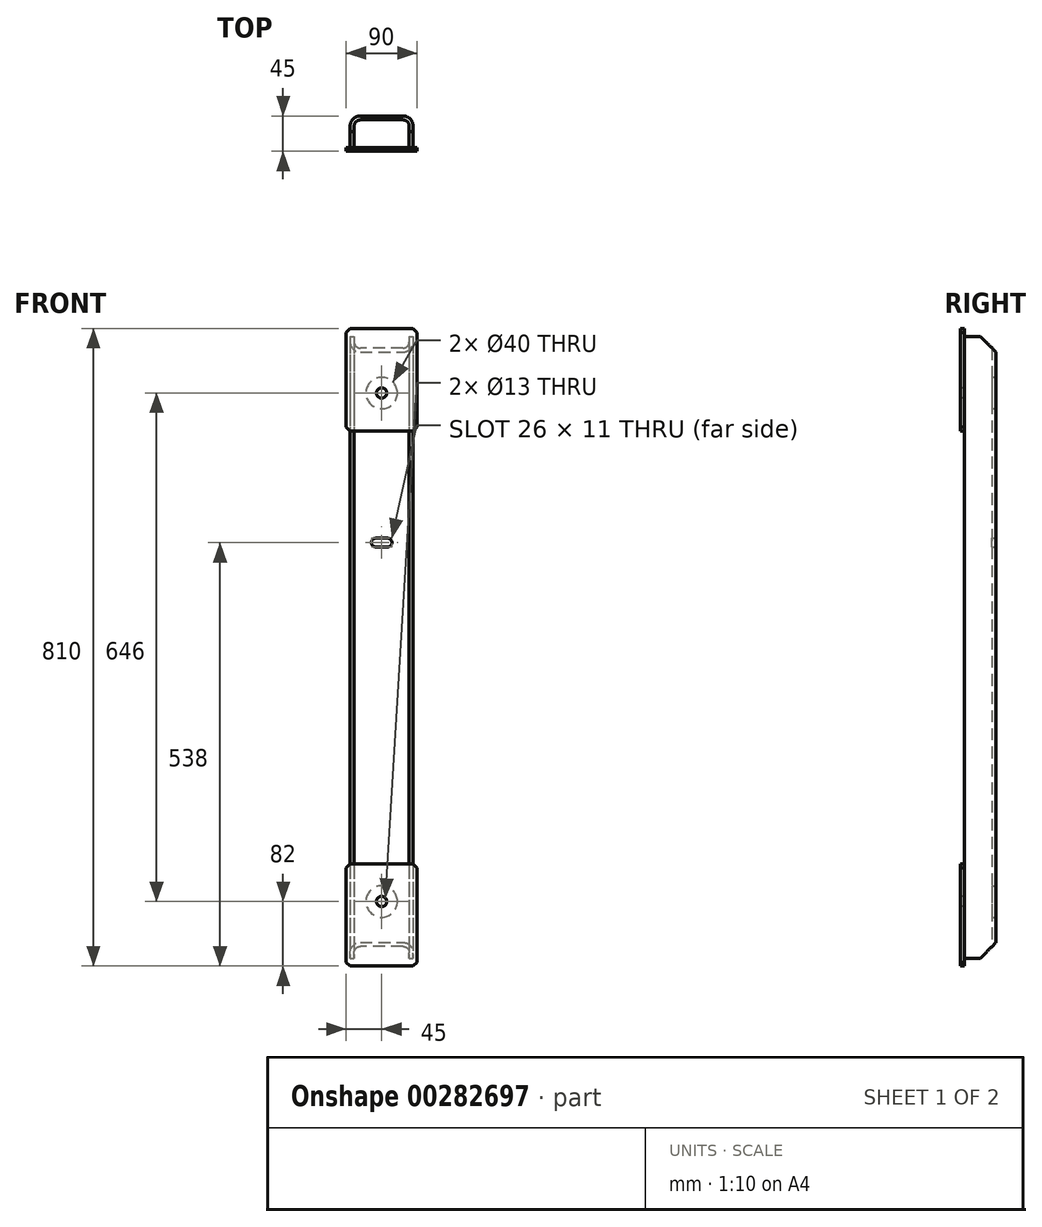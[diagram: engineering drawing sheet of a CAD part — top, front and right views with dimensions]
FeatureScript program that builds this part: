
annotation { "Feature Type Name" : "Feature", "Feature Type Description" : "" }
export const myFeature = defineFeature(function(context is Context, id is Id, definition is map)
    precondition{}
    {
        {
            var Q0;
            Q0=qCreatedBy(makeId("Top.planeOp"),FACE);
            var sketch = newSketch(context, id + "F0", { "sketchPlane" : qUnion([Q0])});
            skLineSegment(sketch, "E0.bottom", {"start": v(-27, 40) * mm, "end": v(27, 40) * mm});
            skLineSegment(sketch, "E0.top", {"start": v(-40, 0) * mm, "end": v(-35, 0) * mm});
            skLineSegment(sketch, "E0.left", {"start": v(-40, 27) * mm, "end": v(-40, 0) * mm});
            skLineSegment(sketch, "E0.right", {"start": v(40, 27) * mm, "end": v(40, 0) * mm});
            skPoint(sketch, "E0.middle", {"position": v(0, 20) * mm});
            skLineSegment(sketch, "E1.0", {"start": v(-27, 35) * mm, "end": v(27, 35) * mm});
            skLineSegment(sketch, "E1.1", {"start": v(-35, 27) * mm, "end": v(-35, 0) * mm});
            skLineSegment(sketch, "E1.3", {"start": v(35, 27) * mm, "end": v(35, 0) * mm});
            skLineSegment(sketch, "E2.trimOffspring", {"start": v(35, 0) * mm, "end": v(40, 0) * mm});
            skPoint(sketch, "E3.visualSharp", {"position": v(-35, 35) * mm});
            skArc(sketch, "E3.filletArc", {"start": v(-27, 35) * mm, "mid": v(-32.66, 32.66) * mm, "end": v(-35, 27) * mm});
            skPoint(sketch, "E4.visualSharp", {"position": v(35, 35) * mm});
            skArc(sketch, "E4.filletArc", {"start": v(35, 27) * mm, "mid": v(32.66, 32.66) * mm, "end": v(27, 35) * mm});
            skPoint(sketch, "E5.visualSharp", {"position": v(-40, 40) * mm});
            skArc(sketch, "E5.filletArc", {"start": v(-27, 40) * mm, "mid": v(-36.2, 36.2) * mm, "end": v(-40, 27) * mm});
            skPoint(sketch, "E6.visualSharp", {"position": v(40, 40) * mm});
            skArc(sketch, "E6.filletArc", {"start": v(40, 27) * mm, "mid": v(36.2, 36.2) * mm, "end": v(27, 40) * mm});
            skSolve(sketch);
        }
        {
            var Q0;
            Q0=makeQuery(id+"F0.imprint","IMPRINT",FACE,{"disambiguationData":[TD([[makeQuery(id+"F0.imprint","IMPRINT",EDGE,{"derivedFrom":sQuery(id+"F0.wireOp",EDGE,"E0.bottom")}),-1.0]])]});
            extrude(context, id + "F1", {"entities" : qUnion([Q0]), "depth" : 790 * mm, "symmetric" : true});
        }
        {
            var Q0;
            Q0=makeQuery(id+"F1.opExtrude","SWEPT_FACE",FACE,{"disambiguationData":[OSD([sQuery(id+"F0.wireOp",EDGE,"E0.bottom")])]});
            var sketch = newSketch(context, id + "F2", { "sketchPlane" : qUnion([Q0])});
            skLineSegment(sketch, "E7", {"start": v(0, 395) * mm, "end": v(0, -395) * mm, "construction": true});
            skCircle(sketch, "E8", {"center": v(0, 323) * mm, "radius": 20 * mm});
            skCircle(sketch, "E9", {"center": v(0, -323) * mm, "radius": 20 * mm});
            skLineSegment(sketch, "E10", {"start": v(79.25, 133) * mm, "end": v(-83.9, 133) * mm, "construction": true});
            skArc(sketch, "E11", {"start": v(7.5, 127.5) * mm, "mid": v(13, 133) * mm, "end": v(7.5, 138.5) * mm});
            skArc(sketch, "E12", {"start": v(-7.5, 138.5) * mm, "mid": v(-13, 133) * mm, "end": v(-7.5, 127.5) * mm});
            skLineSegment(sketch, "E13", {"start": v(7.5, 138.5) * mm, "end": v(-7.5, 138.5) * mm});
            skLineSegment(sketch, "E14", {"start": v(7.5, 127.5) * mm, "end": v(-7.5, 127.5) * mm});
            skArc(sketch, "E15.MirrorCS", {"start": v(-7.5, -138.5) * mm, "mid": v(-13, -133) * mm, "end": v(-7.5, -127.5) * mm});
            skArc(sketch, "E16.MirrorCS", {"start": v(7.5, -127.5) * mm, "mid": v(13, -133) * mm, "end": v(7.5, -138.5) * mm});
            skLineSegment(sketch, "E17.MirrorCS", {"start": v(7.5, -127.5) * mm, "end": v(-7.5, -127.5) * mm});
            skLineSegment(sketch, "E18.MirrorCS", {"start": v(7.5, -138.5) * mm, "end": v(-7.5, -138.5) * mm});
            skSolve(sketch);
        }
        {
            var Q0;
            Q0=makeQuery(id+"F2.imprint","IMPRINT",FACE,{"disambiguationData":[TD([[makeQuery(id+"F2.imprint","IMPRINT",EDGE,{"derivedFrom":sQuery(id+"F2.wireOp",EDGE,"E8")}),1.0]])]});
            var Q1;
            Q1=makeQuery(id+"F2.imprint","IMPRINT",FACE,{"disambiguationData":[TD([[makeQuery(id+"F2.imprint","IMPRINT",EDGE,{"derivedFrom":sQuery(id+"F2.wireOp",EDGE,"E11")}),1.0]])]});
            var Q2;
            Q2=makeQuery(id+"F2.imprint","IMPRINT",FACE,{"disambiguationData":[TD([[makeQuery(id+"F2.imprint","IMPRINT",EDGE,{"derivedFrom":sQuery(id+"F2.wireOp",EDGE,"E15.MirrorCS")}),-1.0]])]});
            var Q3;
            Q3=makeQuery(id+"F2.imprint","IMPRINT",FACE,{"disambiguationData":[TD([[makeQuery(id+"F2.imprint","IMPRINT",EDGE,{"derivedFrom":sQuery(id+"F2.wireOp",EDGE,"E9")}),1.0]])]});
            extrude(context, id + "F3", {"entities" : qUnion([Q0, Q1, Q2, Q3]), "operationType" : NewBodyOperationType.REMOVE, "endBound" : BoundingType.THROUGH_ALL, "oppositeDirection" : true, "depth" : 25 * mm});
        }
        {
            var Q0;
            Q0=makeQuery(id+"F1.opExtrude","SWEPT_FACE",FACE,{"disambiguationData":[OSD([sQuery(id+"F0.wireOp",EDGE,"E0.top")])]});
            var sketch = newSketch(context, id + "F4", { "sketchPlane" : qUnion([Q0])});
            skLineSegment(sketch, "E19.bottom", {"start": v(-45, 405) * mm, "end": v(45, 405) * mm});
            skLineSegment(sketch, "E19.top", {"start": v(-45, 275) * mm, "end": v(45, 275) * mm});
            skLineSegment(sketch, "E19.left", {"start": v(-45, 405) * mm, "end": v(-45, 275) * mm});
            skLineSegment(sketch, "E19.right", {"start": v(45, 405) * mm, "end": v(45, 275) * mm});
            skSolve(sketch);
        }
        {
            var Q0;
            Q0=makeQuery(id+"F4.imprint","IMPRINT",FACE,{"disambiguationData":[TD([[makeQuery(id+"F4.imprint","IMPRINT",EDGE,{"derivedFrom":sQuery(id+"F4.wireOp",EDGE,"E19.bottom")}),-1.0]])]});
            var Q1;
            {var subQ1=sQuery(id+"F0.wireOp",EDGE,"E0.top");var subQ6=makeQuery(id+"F1.opExtrude","CAP_EDGE",EDGE,{"disambiguationData":[OSD([subQ1])],"isStart":false});Q1=makeQuery(id+"F4.imprint","IMPRINT",FACE,{"disambiguationData":[TD([[makeQuery(id+"F4.imprint","IMPRINT",EDGE,{"derivedFrom":subQ6}),-1.0]])]});}
            extrude(context, id + "F5", {"entities" : qUnion([Q0, Q1]), "depth" : 5 * mm});
        }
        {
            var Q0;
            Q0=makeQuery(id+"F5.opExtrude","SWEPT_EDGE",EDGE,{"disambiguationData":[OSD([sQuery(id+"F4.wireOp",EDGE,"E19.top"),sQuery(id+"F4.wireOp",EDGE,"E19.right")])]});
            var Q1;
            Q1=makeQuery(id+"F5.opExtrude","SWEPT_EDGE",EDGE,{"disambiguationData":[OSD([sQuery(id+"F4.wireOp",EDGE,"E19.top"),sQuery(id+"F4.wireOp",EDGE,"E19.left")])]});
            var Q2;
            Q2=makeQuery(id+"F5.opExtrude","SWEPT_EDGE",EDGE,{"disambiguationData":[OSD([sQuery(id+"F4.wireOp",EDGE,"E19.bottom"),sQuery(id+"F4.wireOp",EDGE,"E19.left")])]});
            var Q3;
            Q3=makeQuery(id+"F5.opExtrude","SWEPT_EDGE",EDGE,{"disambiguationData":[OSD([sQuery(id+"F4.wireOp",EDGE,"E19.bottom"),sQuery(id+"F4.wireOp",EDGE,"E19.right")])]});
            chamfer(context, id + "F6", {"entities" : qUnion([Q0, Q1, Q2, Q3]), "width" : 5 * mm, "tangentPropagation" : true});
        }
        {
            var Q0;
            Q0=makeQuery(id+"F5.opExtrude","CAP_FACE",FACE,{"disambiguationData":[OSD([sQuery(id+"F4.wireOp",EDGE,"E19.bottom"),sQuery(id+"F4.wireOp",EDGE,"E19.top"),sQuery(id+"F4.wireOp",EDGE,"E19.left"),sQuery(id+"F4.wireOp",EDGE,"E19.right")])],"isStart":false});
            var sketch = newSketch(context, id + "F7", { "sketchPlane" : qUnion([Q0])});
            skCircle(sketch, "E20.0", {"center": v(0, 323) * mm, "radius": 20 * mm});
            skCircle(sketch, "E21", {"center": v(0, 323) * mm, "radius": 6.5 * mm});
            skSolve(sketch);
        }
        {
            var Q0;
            Q0=makeQuery(id+"F7.imprint","IMPRINT",FACE,{"disambiguationData":[TD([[makeQuery(id+"F7.imprint","IMPRINT",EDGE,{"derivedFrom":sQuery(id+"F7.wireOp",EDGE,"E21")}),1.0]])]});
            extrude(context, id + "F8", {"entities" : qUnion([Q0]), "operationType" : NewBodyOperationType.REMOVE, "endBound" : BoundingType.THROUGH_ALL, "oppositeDirection" : true, "depth" : 25 * mm});
        }
        {
            var Q0;
            Q0=makeQuery(id+"F5.opExtrude","SWEPT_BODY",BODY,{"disambiguationData":[OSD([sQuery(id+"F4.wireOp",EDGE,"E19.bottom"),sQuery(id+"F4.wireOp",EDGE,"E19.top"),sQuery(id+"F4.wireOp",EDGE,"E19.left"),sQuery(id+"F4.wireOp",EDGE,"E19.right")])]});
            var Q1;
            Q1=qCreatedBy(makeId("Top.planeOp"),FACE);
            mirror(context, id + "F9", {"operationType" : NewBodyOperationType.ADD, "entities" : qUnion([Q0]), "mirrorPlane" : qUnion([Q1])});
        }
        {
            var Q0;
            Q0=makeQuery(id+"F1.opExtrude","SWEPT_FACE",FACE,{"disambiguationData":[OSD([sQuery(id+"F0.wireOp",EDGE,"E0.right")])]});
            var sketch = newSketch(context, id + "F10", { "sketchPlane" : qUnion([Q0])});
            skLineSegment(sketch, "E22.0", {"start": v(40, 395) * mm, "end": v(20, 395) * mm});
            skLineSegment(sketch, "E22.1", {"start": v(40, 395) * mm, "end": v(40, 375) * mm});
            skPoint(sketch, "E23.orphan", {"position": v(27, 395) * mm});
            skLineSegment(sketch, "E24", {"start": v(20, 395) * mm, "end": v(40, 375) * mm});
            skPoint(sketch, "E25.orphan", {"position": v(40, -395) * mm});
            skPoint(sketch, "E26.orphan", {"position": v(0, 395) * mm});
            skLineSegment(sketch, "E27.MirrorCS", {"start": v(40, -395) * mm, "end": v(20, -395) * mm});
            skPoint(sketch, "E28.MirrorP", {"position": v(0, -395) * mm});
            skLineSegment(sketch, "E29.MirrorCS", {"start": v(20, -395) * mm, "end": v(40, -375) * mm});
            skPoint(sketch, "E30.MirrorP", {"position": v(27, -395) * mm});
            skLineSegment(sketch, "E31.MirrorCS", {"start": v(40, -395) * mm, "end": v(40, -375) * mm});
            skSolve(sketch);
        }
        {
            var Q0;
            {var subQ0=sQuery(id+"F10.wireOp",EDGE,"E22.0");var subQ1=sQuery(id+"F0.wireOp",EDGE,"E0.right");var subQ2=makeQuery(id+"F1.opExtrude","SWEPT_EDGE",EDGE,{"disambiguationData":[OSD([subQ1,sQuery(id+"F0.wireOp",EDGE,"E6.filletArc")])]});var subQ3=makeQuery(id+"F10.imprint","INTERSECT",VERTEX,{"derivedFrom":[subQ2,subQ0]});Q0=makeQuery(id+"F10.imprint","IMPRINT",FACE,{"disambiguationData":[TD([[makeQuery(id+"F10.imprint","IMPRINT",EDGE,{"disambiguationData":[TD([[subQ3,-1.0]])],"derivedFrom":subQ0}),1.0]])]});}
            var Q1;
            {var subQ3=sQuery(id+"F10.wireOp",EDGE,"E22.1");Q1=makeQuery(id+"F10.imprint","IMPRINT",FACE,{"disambiguationData":[TD([[makeQuery(id+"F10.imprint","IMPRINT",EDGE,{"derivedFrom":subQ3}),-1.0]])]});}
            var Q2;
            {var subQ0=sQuery(id+"F10.wireOp",EDGE,"E27.MirrorCS");var subQ1=sQuery(id+"F0.wireOp",EDGE,"E0.right");var subQ2=makeQuery(id+"F1.opExtrude","SWEPT_EDGE",EDGE,{"disambiguationData":[OSD([subQ1,sQuery(id+"F0.wireOp",EDGE,"E6.filletArc")])]});var subQ3=makeQuery(id+"F10.imprint","INTERSECT",VERTEX,{"derivedFrom":[subQ2,subQ0]});Q2=makeQuery(id+"F10.imprint","IMPRINT",FACE,{"disambiguationData":[TD([[makeQuery(id+"F10.imprint","IMPRINT",EDGE,{"disambiguationData":[TD([[subQ3,-1.0]])],"derivedFrom":subQ0}),-1.0]])]});}
            var Q3;
            {var subQ3=sQuery(id+"F10.wireOp",EDGE,"E31.MirrorCS");Q3=makeQuery(id+"F10.imprint","IMPRINT",FACE,{"disambiguationData":[TD([[makeQuery(id+"F10.imprint","IMPRINT",EDGE,{"derivedFrom":subQ3}),1.0]])]});}
            extrude(context, id + "F11", {"entities" : qUnion([Q0, Q1, Q2, Q3]), "operationType" : NewBodyOperationType.REMOVE, "endBound" : BoundingType.THROUGH_ALL, "oppositeDirection" : true, "depth" : 25 * mm});
        }
    });
